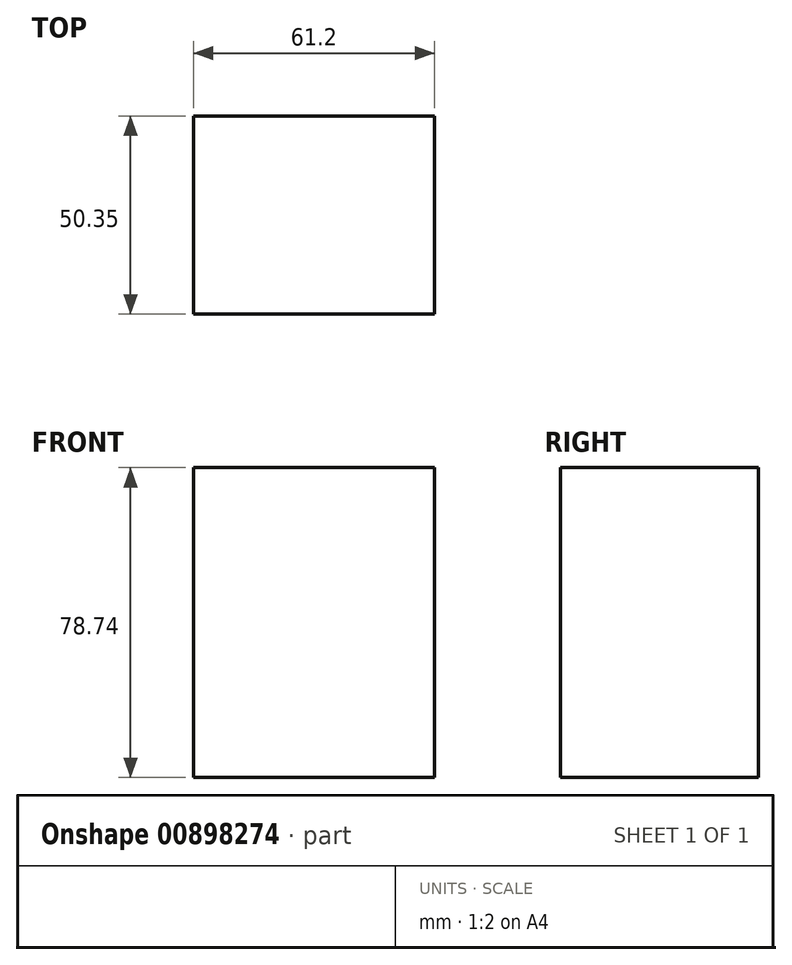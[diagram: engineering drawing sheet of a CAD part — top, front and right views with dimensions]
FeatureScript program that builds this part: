
annotation { "Feature Type Name" : "Feature", "Feature Type Description" : "" }
export const myFeature = defineFeature(function(context is Context, id is Id, definition is map)
    precondition{}
    {
        {
            var Q0;
            Q0=qCreatedBy(makeId("Top.planeOp"),FACE);
            var sketch = newSketch(context, id + "F0", { "sketchPlane" : qUnion([Q0])});
            skLineSegment(sketch, "E0.bottom", {"start": v(0, 0) * mm, "end": v(61.2, 0) * mm});
            skLineSegment(sketch, "E0.top", {"start": v(0, 50.35) * mm, "end": v(61.2, 50.35) * mm});
            skLineSegment(sketch, "E0.left", {"start": v(0, 0) * mm, "end": v(0, 50.35) * mm});
            skLineSegment(sketch, "E0.right", {"start": v(61.2, 0) * mm, "end": v(61.2, 50.35) * mm});
            skSolve(sketch);
        }
        {
            var Q0;
            Q0=makeQuery(id+"F0.imprint","IMPRINT",FACE,{"disambiguationData":[TD([[makeQuery(id+"F0.imprint","IMPRINT",EDGE,{"derivedFrom":sQuery(id+"F0.wireOp",EDGE,"E0.bottom")}),1.0]])]});
            extrude(context, id + "F1", {"entities" : qUnion([Q0]), "depth" : 78.74 * mm, "offsetDistance" : 25.4 * mm});
        }
    });
